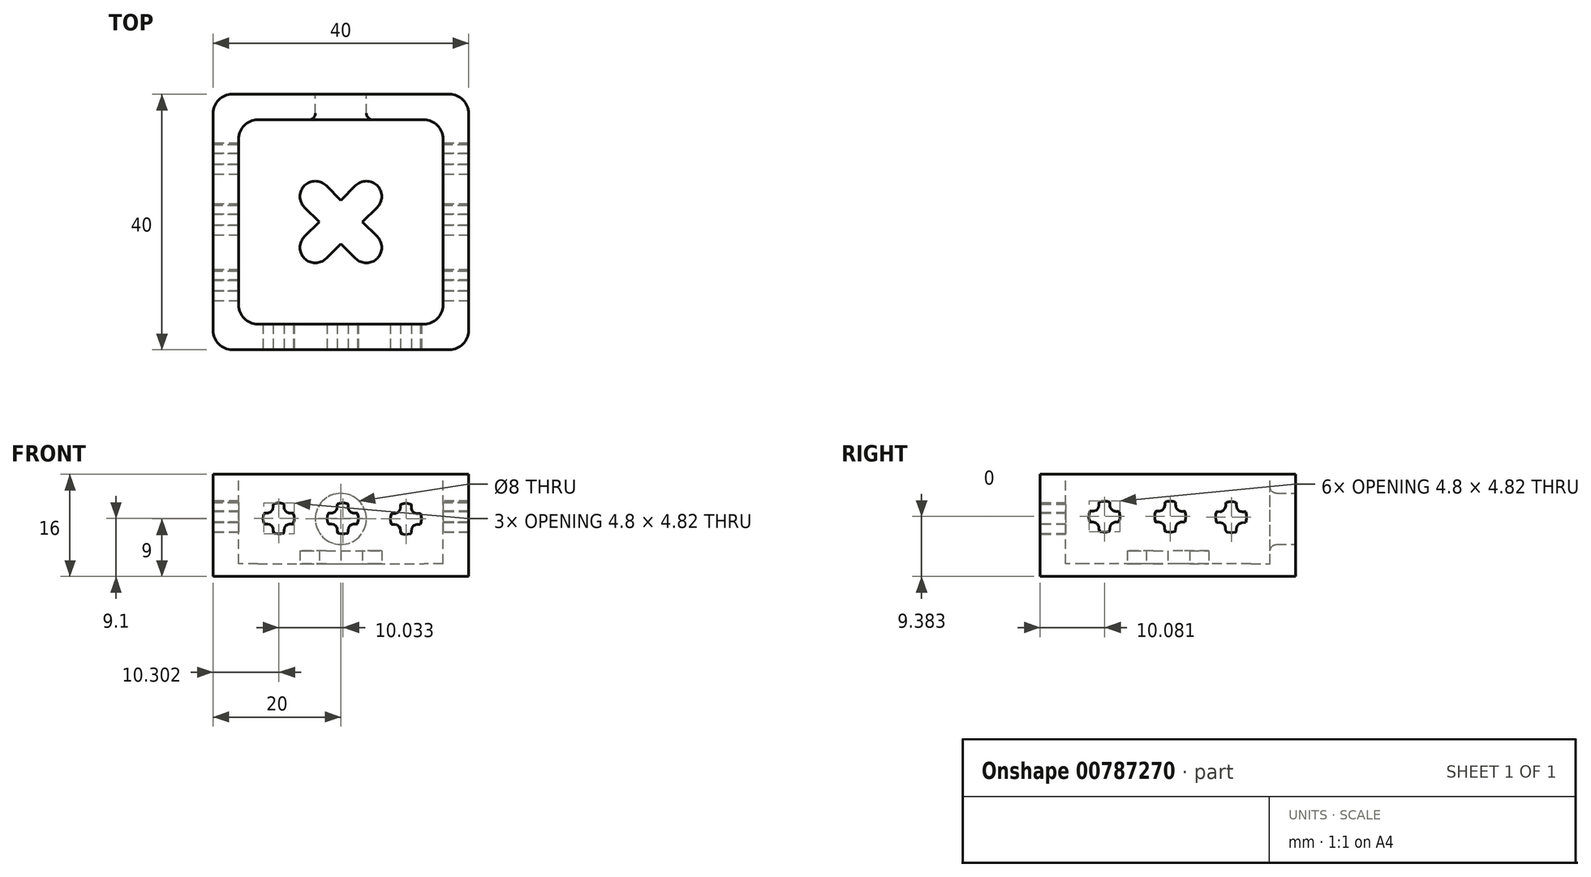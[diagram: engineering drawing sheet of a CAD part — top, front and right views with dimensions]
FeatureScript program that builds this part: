
annotation { "Feature Type Name" : "Feature", "Feature Type Description" : "" }
export const myFeature = defineFeature(function(context is Context, id is Id, definition is map)
    precondition{}
    {
        {
            var Q0;
            Q0=qCreatedBy(makeId("Top.planeOp"),FACE);
            var sketch = newSketch(context, id + "F0", { "sketchPlane" : qUnion([Q0])});
            skArc(sketch, "E0", {"start": v(1.7, 1.7) * mm, "mid": v(-1.7, 1.7) * mm, "end": v(-1.7, -1.7) * mm});
            skArc(sketch, "E1", {"start": v(9.7, -1.7) * mm, "mid": v(9.7, 1.7) * mm, "end": v(6.3, 1.7) * mm});
            skArc(sketch, "E2", {"start": v(6.3, -9.7) * mm, "mid": v(9.7, -9.7) * mm, "end": v(9.7, -6.3) * mm});
            skArc(sketch, "E3", {"start": v(-1.7, -6.3) * mm, "mid": v(-1.7, -9.7) * mm, "end": v(1.7, -9.7) * mm});
            skLineSegment(sketch, "E4", {"start": v(-1.7, -6.3) * mm, "end": v(0.6, -4) * mm});
            skLineSegment(sketch, "E5", {"start": v(9.7, -6.3) * mm, "end": v(7.4, -4) * mm});
            skLineSegment(sketch, "E6", {"start": v(-1.7, -1.7) * mm, "end": v(0.6, -4) * mm});
            skLineSegment(sketch, "E7", {"start": v(1.7, -9.7) * mm, "end": v(4, -7.4) * mm});
            skLineSegment(sketch, "E8.trimOffspring", {"start": v(4, -7.4) * mm, "end": v(6.3, -9.7) * mm});
            skLineSegment(sketch, "E9.trimOffspring", {"start": v(4, -0.6) * mm, "end": v(6.3, 1.7) * mm});
            skLineSegment(sketch, "E10.trimOffspring", {"start": v(4, -0.6) * mm, "end": v(1.7, 1.7) * mm});
            skLineSegment(sketch, "E11.trimOffspring", {"start": v(7.4, -4) * mm, "end": v(9.7, -1.7) * mm});
            skSolve(sketch);
        }
        {
            var Q0;
            Q0=makeQuery(id+"F0.imprint","IMPRINT",FACE,{"disambiguationData":[TD([[makeQuery(id+"F0.imprint","IMPRINT",EDGE,{"derivedFrom":sQuery(id+"F0.wireOp",EDGE,"E0")}),1.0]])]});
            extrude(context, id + "F1", {"entities" : qUnion([Q0]), "depth" : 2 * mm, "offsetDistance" : 25 * mm});
        }
        {
            var Q0;
            Q0=qCreatedBy(makeId("Top.planeOp"),FACE);
            var sketch = newSketch(context, id + "F2", { "sketchPlane" : qUnion([Q0])});
            skLineSegment(sketch, "E12.bottom", {"start": v(-9, 12) * mm, "end": v(17, 12) * mm});
            skLineSegment(sketch, "E12.top", {"start": v(-9, -20) * mm, "end": v(17, -20) * mm});
            skLineSegment(sketch, "E12.left", {"start": v(-12, 9) * mm, "end": v(-12, -17) * mm});
            skLineSegment(sketch, "E12.right", {"start": v(20, 9) * mm, "end": v(20, -17) * mm});
            skLineSegment(sketch, "E13", {"start": v(0.6, -4) * mm, "end": v(7.4, -4) * mm});
            skLineSegment(sketch, "E14", {"start": v(4, -0.6) * mm, "end": v(4, -7.4) * mm});
            skPoint(sketch, "E15", {"position": v(4, -4) * mm});
            skPoint(sketch, "E16", {"position": v(-12, -4) * mm});
            skPoint(sketch, "E17", {"position": v(4, 12) * mm});
            skPoint(sketch, "E18.visualSharp", {"position": v(20, 12) * mm});
            skArc(sketch, "E18.filletArc", {"start": v(20, 9) * mm, "mid": v(19.12, 11.12) * mm, "end": v(17, 12) * mm});
            skPoint(sketch, "E19.visualSharp", {"position": v(20, -20) * mm});
            skArc(sketch, "E19.filletArc", {"start": v(17, -20) * mm, "mid": v(19.12, -19.12) * mm, "end": v(20, -17) * mm});
            skPoint(sketch, "E20.visualSharp", {"position": v(-12, 12) * mm});
            skArc(sketch, "E20.filletArc", {"start": v(-9, 12) * mm, "mid": v(-11.12, 11.12) * mm, "end": v(-12, 9) * mm});
            skPoint(sketch, "E21.visualSharp", {"position": v(-12, -20) * mm});
            skArc(sketch, "E21.filletArc", {"start": v(-12, -17) * mm, "mid": v(-11.12, -19.12) * mm, "end": v(-9, -20) * mm});
            skLineSegment(sketch, "E22.bottom", {"start": v(-16, 16) * mm, "end": v(24, 16) * mm});
            skLineSegment(sketch, "E22.top", {"start": v(-16, -24) * mm, "end": v(24, -24) * mm});
            skLineSegment(sketch, "E22.left", {"start": v(-16, 16) * mm, "end": v(-16, -24) * mm});
            skLineSegment(sketch, "E22.right", {"start": v(24, 16) * mm, "end": v(24, -24) * mm});
            skPoint(sketch, "E23", {"position": v(-16, -4) * mm});
            skPoint(sketch, "E24", {"position": v(24, -4) * mm});
            skPoint(sketch, "E25", {"position": v(4, 16) * mm});
            skSolve(sketch);
        }
        {
            var Q0;
            Q0=makeQuery(id+"F2.imprint","IMPRINT",FACE,{"disambiguationData":[TD([[makeQuery(id+"F2.imprint","IMPRINT",EDGE,{"derivedFrom":sQuery(id+"F2.wireOp",EDGE,"E12.bottom")}),1.0]])]});
            extrude(context, id + "F3", {"entities" : qUnion([Q0]), "oppositeDirection" : true, "depth" : 2 * mm, "offsetDistance" : 25 * mm, "hasSecondDirection" : true, "secondDirectionOppositeDirection" : false, "secondDirectionDepth" : 14 * mm});
        }
        {
            var Q0;
            Q0=makeQuery(id+"F2.imprint","IMPRINT",FACE,{"disambiguationData":[TD([[makeQuery(id+"F2.imprint","IMPRINT",EDGE,{"derivedFrom":sQuery(id+"F2.wireOp",EDGE,"E12.bottom")}),-1.0]])]});
            var Q1;
            Q1=sQuery(id+"F2.wireOp",EDGE,"E20.filletArc");
            var Q2;
            Q2=sQuery(id+"F2.wireOp",EDGE,"E12.bottom");
            var Q3;
            Q3=sQuery(id+"F2.wireOp",EDGE,"E18.filletArc");
            var Q4;
            Q4=sQuery(id+"F2.wireOp",EDGE,"E12.right");
            var Q5;
            Q5=sQuery(id+"F2.wireOp",EDGE,"E19.filletArc");
            var Q6;
            Q6=sQuery(id+"F2.wireOp",EDGE,"E12.top");
            var Q7;
            Q7=sQuery(id+"F2.wireOp",EDGE,"E21.filletArc");
            var Q8;
            Q8=sQuery(id+"F2.wireOp",EDGE,"E12.left");
            extrude(context, id + "F4", {"entities" : qUnion([Q0]), "operationType" : NewBodyOperationType.ADD, "surfaceEntities" : qUnion([Q1, Q2, Q3, Q4, Q5, Q6, Q7, Q8]), "oppositeDirection" : true, "depth" : 2 * mm, "offsetDistance" : 25 * mm});
        }
        {
            var Q0;
            Q0=makeQuery(id+"F3.opExtrude","SWEPT_EDGE",EDGE,{"disambiguationData":[OSD([sQuery(id+"F2.wireOp",EDGE,"E22.top"),sQuery(id+"F2.wireOp",EDGE,"E22.left")])]});
            var Q1;
            Q1=makeQuery(id+"F3.opExtrude","SWEPT_EDGE",EDGE,{"disambiguationData":[OSD([sQuery(id+"F2.wireOp",EDGE,"E22.bottom"),sQuery(id+"F2.wireOp",EDGE,"E22.left")])]});
            var Q2;
            Q2=makeQuery(id+"F3.opExtrude","SWEPT_EDGE",EDGE,{"disambiguationData":[OSD([sQuery(id+"F2.wireOp",EDGE,"E22.bottom"),sQuery(id+"F2.wireOp",EDGE,"E22.right")])]});
            var Q3;
            Q3=makeQuery(id+"F3.opExtrude","SWEPT_EDGE",EDGE,{"disambiguationData":[OSD([sQuery(id+"F2.wireOp",EDGE,"E22.top"),sQuery(id+"F2.wireOp",EDGE,"E22.right")])]});
            fillet(context, id + "F5", {"entities" : qUnion([Q0, Q1, Q2, Q3]), "radius" : 3 * mm, "tangentPropagation" : true, "allowEdgeOverflow" : false});
        }
        {
            var Q0;
            Q0=makeQuery(id+"F3.opExtrude","SWEPT_FACE",FACE,{"disambiguationData":[OSD([sQuery(id+"F2.wireOp",EDGE,"E22.bottom")])]});
            var sketch = newSketch(context, id + "F6", { "sketchPlane" : qUnion([Q0])});
            skCircle(sketch, "E26", {"center": v(-4, 7) * mm, "radius": 4 * mm});
            skLineSegment(sketch, "E27", {"start": v(-20, 0) * mm, "end": v(-20, 14) * mm});
            skPoint(sketch, "E28", {"position": v(-20, 7) * mm});
            skLineSegment(sketch, "E29", {"start": v(-24, 14) * mm, "end": v(16, 14) * mm});
            skPoint(sketch, "E30", {"position": v(-4, 14) * mm});
            skSolve(sketch);
        }
        {
            var Q0;
            Q0=makeQuery(id+"F6.imprint","IMPRINT",FACE,{"disambiguationData":[TD([[makeQuery(id+"F6.imprint","IMPRINT",EDGE,{"derivedFrom":sQuery(id+"F6.wireOp",EDGE,"E26")}),1.0]])]});
            extrude(context, id + "F7", {"entities" : qUnion([Q0]), "operationType" : NewBodyOperationType.REMOVE, "oppositeDirection" : true, "depth" : 25 * mm, "offsetDistance" : 25 * mm});
        }
        {
            var Q0;
            Q0=makeQuery(id+"F7.boolean.opBoolean","COPY",EDGE,{"derivedFrom":makeQuery(id+"F7.opExtrude","CAP_EDGE",EDGE,{"disambiguationData":[OSD([sQuery(id+"F6.wireOp",EDGE,"E26")])],"isStart":true})});
            var Q1;
            Q1=makeQuery(id+"F7.boolean.opBoolean","INTERSECT",EDGE,{"derivedFrom":[makeQuery(id+"F3.opExtrude","SWEPT_FACE",FACE,{"disambiguationData":[OSD([sQuery(id+"F2.wireOp",EDGE,"E12.bottom")])]}),makeQuery(id+"F7.opExtrude","SWEPT_FACE",FACE,{"disambiguationData":[OSD([sQuery(id+"F6.wireOp",EDGE,"E26")])]})]});
            fillet(context, id + "F8", {"entities" : qUnion([Q0, Q1]), "radius" : 1 * mm, "tangentPropagation" : true, "allowEdgeOverflow" : false});
        }
        {
            var Q0;
            Q0=makeQuery(id+"F3.opExtrude","SWEPT_FACE",FACE,{"disambiguationData":[OSD([sQuery(id+"F2.wireOp",EDGE,"E22.top")])]});
            var sketch = newSketch(context, id + "F9", { "sketchPlane" : qUnion([Q0])});
            skFitSpline(sketch, "E31", {"points": [v(-6.58, 9.34) * mm, v(-5.7, 9.51) * mm, v(-4.88, 9.34) * mm], "startDerivative": vector(1.75, 0.5) * mm, "endDerivative": vector(1.65, -0.5) * mm});
            skFitSpline(sketch, "E32", {"points": [v(-4.88, 9.34) * mm, v(-4.88, 8.78) * mm, v(-4.74, 8.34) * mm, v(-4.42, 8.05) * mm, v(-4.08, 7.93) * mm, v(-3.66, 7.92) * mm, v(-3.46, 7.92) * mm, v(-3.38, 7.68) * mm, v(-3.3, 7.3) * mm, v(-3.3, 6.95) * mm, v(-3.34, 6.64) * mm, v(-3.46, 6.22) * mm], "startDerivative": vector(-0.26, -5.18) * mm, "endDerivative": vector(-1.41, -4.37) * mm});
            skFitSpline(sketch, "E33", {"points": [v(-6.58, 9.34) * mm, v(-6.58, 9.05) * mm, v(-6.59, 8.8) * mm, v(-6.61, 8.61) * mm, v(-6.79, 8.27) * mm, v(-6.98, 8.09) * mm, v(-7.24, 7.96) * mm, v(-7.56, 7.92) * mm, v(-8, 7.92) * mm, v(-8.1, 7.64) * mm, v(-8.15, 7.36) * mm, v(-8.17, 7.03) * mm, v(-8.14, 6.74) * mm, v(-8.09, 6.47) * mm, v(-8, 6.22) * mm, v(-7.81, 6.22) * mm, v(-7.5, 6.22) * mm, v(-7.25, 6.19) * mm, v(-7.06, 6.1) * mm, v(-6.84, 5.93) * mm, v(-6.73, 5.8) * mm, v(-6.64, 5.61) * mm, v(-6.59, 5.37) * mm, v(-6.58, 5.12) * mm, v(-6.58, 4.8) * mm, v(-6.33, 4.72) * mm, v(-5.98, 4.66) * mm, v(-5.7, 4.65) * mm, v(-5.43, 4.67) * mm, v(-5.07, 4.74) * mm, v(-4.88, 4.8) * mm, v(-4.88, 5.12) * mm, v(-4.88, 5.4) * mm, v(-4.78, 5.73) * mm, v(-4.64, 5.92) * mm, v(-4.37, 6.12) * mm, v(-3.96, 6.22) * mm, v(-3.46, 6.22) * mm], "startDerivative": vector(-0.02, -10.87) * mm, "endDerivative": vector(14.17, -0.52) * mm});
            skFitSpline(sketch, "E34", {"points": [v(3.45, 9.34) * mm, v(4.33, 9.51) * mm, v(5.15, 9.34) * mm], "startDerivative": vector(1.75, 0.5) * mm, "endDerivative": vector(1.65, -0.5) * mm});
            skFitSpline(sketch, "E35", {"points": [v(5.15, 9.34) * mm, v(5.15, 8.78) * mm, v(5.3, 8.34) * mm, v(5.61, 8.05) * mm, v(5.95, 7.93) * mm, v(6.37, 7.92) * mm, v(6.57, 7.92) * mm, v(6.65, 7.68) * mm, v(6.73, 7.3) * mm, v(6.73, 6.95) * mm, v(6.7, 6.64) * mm, v(6.57, 6.22) * mm], "startDerivative": vector(-0.26, -5.18) * mm, "endDerivative": vector(-1.41, -4.37) * mm});
            skFitSpline(sketch, "E36", {"points": [v(3.45, 9.34) * mm, v(3.45, 9.05) * mm, v(3.45, 8.8) * mm, v(3.42, 8.61) * mm, v(3.25, 8.27) * mm, v(3.05, 8.09) * mm, v(2.79, 7.96) * mm, v(2.47, 7.92) * mm, v(2.03, 7.92) * mm, v(1.94, 7.64) * mm, v(1.88, 7.36) * mm, v(1.86, 7.03) * mm, v(1.89, 6.74) * mm, v(1.95, 6.47) * mm, v(2.03, 6.22) * mm, v(2.22, 6.22) * mm, v(2.54, 6.22) * mm, v(2.79, 6.19) * mm, v(2.97, 6.1) * mm, v(3.2, 5.93) * mm, v(3.3, 5.8) * mm, v(3.4, 5.61) * mm, v(3.45, 5.37) * mm, v(3.45, 5.12) * mm, v(3.45, 4.8) * mm, v(3.7, 4.72) * mm, v(4.05, 4.66) * mm, v(4.33, 4.65) * mm, v(4.6, 4.67) * mm, v(4.96, 4.74) * mm, v(5.15, 4.8) * mm, v(5.15, 5.12) * mm, v(5.15, 5.4) * mm, v(5.25, 5.73) * mm, v(5.4, 5.92) * mm, v(5.66, 6.12) * mm, v(6.07, 6.22) * mm, v(6.57, 6.22) * mm], "startDerivative": vector(-0.02, -10.87) * mm, "endDerivative": vector(14.17, -0.52) * mm});
            skFitSpline(sketch, "E37", {"points": [v(13.33, 9.26) * mm, v(14.21, 9.43) * mm, v(15.03, 9.26) * mm], "startDerivative": vector(1.75, 0.5) * mm, "endDerivative": vector(1.65, -0.5) * mm});
            skFitSpline(sketch, "E38", {"points": [v(15.03, 9.26) * mm, v(15.03, 8.7) * mm, v(15.18, 8.27) * mm, v(15.5, 7.97) * mm, v(15.83, 7.85) * mm, v(16.25, 7.84) * mm, v(16.45, 7.84) * mm, v(16.53, 7.6) * mm, v(16.6, 7.22) * mm, v(16.61, 6.88) * mm, v(16.57, 6.56) * mm, v(16.45, 6.14) * mm], "startDerivative": vector(-0.26, -5.18) * mm, "endDerivative": vector(-1.41, -4.37) * mm});
            skFitSpline(sketch, "E39", {"points": [v(13.33, 9.26) * mm, v(13.33, 8.97) * mm, v(13.33, 8.72) * mm, v(13.3, 8.53) * mm, v(13.13, 8.2) * mm, v(12.93, 8) * mm, v(12.67, 7.88) * mm, v(12.35, 7.84) * mm, v(11.9, 7.84) * mm, v(11.82, 7.56) * mm, v(11.76, 7.28) * mm, v(11.74, 6.95) * mm, v(11.77, 6.66) * mm, v(11.83, 6.4) * mm, v(11.9, 6.14) * mm, v(12.1, 6.14) * mm, v(12.42, 6.14) * mm, v(12.66, 6.1) * mm, v(12.85, 6.03) * mm, v(13.08, 5.85) * mm, v(13.18, 5.71) * mm, v(13.27, 5.54) * mm, v(13.33, 5.29) * mm, v(13.33, 5.04) * mm, v(13.33, 4.72) * mm, v(13.58, 4.64) * mm, v(13.93, 4.58) * mm, v(14.21, 4.57) * mm, v(14.48, 4.59) * mm, v(14.84, 4.66) * mm, v(15.03, 4.72) * mm, v(15.03, 5.04) * mm, v(15.03, 5.32) * mm, v(15.13, 5.65) * mm, v(15.27, 5.84) * mm, v(15.54, 6.04) * mm, v(15.95, 6.14) * mm, v(16.45, 6.14) * mm], "startDerivative": vector(-0.02, -10.87) * mm, "endDerivative": vector(14.17, -0.52) * mm});
            skSolve(sketch);
        }
        {
            var Q0;
            Q0=makeQuery(id+"F9.imprint","IMPRINT",FACE,{"disambiguationData":[TD([[makeQuery(id+"F9.imprint","IMPRINT",EDGE,{"derivedFrom":sQuery(id+"F9.wireOp",EDGE,"E31")}),-1.0]])]});
            var Q1;
            Q1=makeQuery(id+"F9.imprint","IMPRINT",FACE,{"disambiguationData":[TD([[makeQuery(id+"F9.imprint","IMPRINT",EDGE,{"derivedFrom":sQuery(id+"F9.wireOp",EDGE,"E34")}),-1.0]])]});
            var Q2;
            Q2=makeQuery(id+"F9.imprint","IMPRINT",FACE,{"disambiguationData":[TD([[makeQuery(id+"F9.imprint","IMPRINT",EDGE,{"derivedFrom":sQuery(id+"F9.wireOp",EDGE,"E37")}),-1.0]])]});
            var Q3;
            Q3=sQuery(id+"F9.wireOp",EDGE,"E39");
            var Q4;
            Q4=sQuery(id+"F9.wireOp",EDGE,"E36");
            var Q5;
            Q5=sQuery(id+"F9.wireOp",EDGE,"E35");
            var Q6;
            Q6=sQuery(id+"F9.wireOp",EDGE,"E33");
            var Q7;
            Q7=sQuery(id+"F9.wireOp",EDGE,"E38");
            var Q8;
            Q8=sQuery(id+"F9.wireOp",EDGE,"E34");
            var Q9;
            Q9=sQuery(id+"F9.wireOp",EDGE,"E32");
            var Q10;
            Q10=sQuery(id+"F9.wireOp",EDGE,"E31");
            var Q11;
            Q11=sQuery(id+"F9.wireOp",EDGE,"E37");
            extrude(context, id + "F10", {"entities" : qUnion([Q0, Q1, Q2]), "operationType" : NewBodyOperationType.REMOVE, "surfaceEntities" : qUnion([Q3, Q4, Q5, Q6, Q7, Q8, Q9, Q10, Q11]), "oppositeDirection" : true, "depth" : 25 * mm, "offsetDistance" : 25 * mm});
        }
        {
            var Q0;
            Q0=makeQuery(id+"F3.opExtrude","SWEPT_FACE",FACE,{"disambiguationData":[OSD([sQuery(id+"F2.wireOp",EDGE,"E22.right")])]});
            var sketch = newSketch(context, id + "F11", { "sketchPlane" : qUnion([Q0])});
            skFitSpline(sketch, "E40", {"points": [v(-14.8, 9.63) * mm, v(-13.92, 9.8) * mm, v(-13.1, 9.63) * mm], "startDerivative": vector(1.75, 0.5) * mm, "endDerivative": vector(1.65, -0.5) * mm});
            skFitSpline(sketch, "E41", {"points": [v(-13.1, 9.63) * mm, v(-13.1, 9.06) * mm, v(-12.96, 8.63) * mm, v(-12.64, 8.33) * mm, v(-12.3, 8.21) * mm, v(-11.88, 8.2) * mm, v(-11.68, 8.2) * mm, v(-11.6, 7.96) * mm, v(-11.53, 7.58) * mm, v(-11.52, 7.24) * mm, v(-11.56, 6.92) * mm, v(-11.68, 6.5) * mm], "startDerivative": vector(-0.26, -5.18) * mm, "endDerivative": vector(-1.41, -4.37) * mm});
            skFitSpline(sketch, "E42", {"points": [v(-14.8, 9.63) * mm, v(-14.8, 9.33) * mm, v(-14.8, 9.09) * mm, v(-14.84, 8.9) * mm, v(-15, 8.55) * mm, v(-15.2, 8.37) * mm, v(-15.47, 8.24) * mm, v(-15.78, 8.2) * mm, v(-16.23, 8.2) * mm, v(-16.31, 7.93) * mm, v(-16.37, 7.64) * mm, v(-16.4, 7.31) * mm, v(-16.37, 7.02) * mm, v(-16.3, 6.76) * mm, v(-16.23, 6.5) * mm, v(-16.03, 6.5) * mm, v(-15.72, 6.5) * mm, v(-15.47, 6.47) * mm, v(-15.28, 6.39) * mm, v(-15.06, 6.22) * mm, v(-14.95, 6.08) * mm, v(-14.86, 5.9) * mm, v(-14.8, 5.65) * mm, v(-14.8, 5.4) * mm, v(-14.8, 5.09) * mm, v(-14.55, 5) * mm, v(-14.2, 4.94) * mm, v(-13.92, 4.93) * mm, v(-13.66, 4.95) * mm, v(-13.29, 5.02) * mm, v(-13.1, 5.09) * mm, v(-13.1, 5.4) * mm, v(-13.1, 5.68) * mm, v(-13, 6) * mm, v(-12.86, 6.2) * mm, v(-12.6, 6.4) * mm, v(-12.18, 6.5) * mm, v(-11.68, 6.5) * mm], "startDerivative": vector(-0.02, -10.87) * mm, "endDerivative": vector(14.17, -0.52) * mm});
            skFitSpline(sketch, "E43", {"points": [v(-4.5, 9.63) * mm, v(-3.62, 9.8) * mm, v(-2.8, 9.63) * mm], "startDerivative": vector(1.75, 0.5) * mm, "endDerivative": vector(1.65, -0.5) * mm});
            skFitSpline(sketch, "E44", {"points": [v(-2.8, 9.63) * mm, v(-2.8, 9.06) * mm, v(-2.65, 8.63) * mm, v(-2.34, 8.33) * mm, v(-2, 8.21) * mm, v(-1.58, 8.2) * mm, v(-1.38, 8.2) * mm, v(-1.3, 7.96) * mm, v(-1.23, 7.58) * mm, v(-1.22, 7.24) * mm, v(-1.26, 6.92) * mm, v(-1.38, 6.5) * mm], "startDerivative": vector(-0.26, -5.18) * mm, "endDerivative": vector(-1.41, -4.37) * mm});
            skFitSpline(sketch, "E45", {"points": [v(-4.5, 9.63) * mm, v(-4.5, 9.33) * mm, v(-4.5, 9.09) * mm, v(-4.53, 8.9) * mm, v(-4.7, 8.55) * mm, v(-4.9, 8.37) * mm, v(-5.16, 8.24) * mm, v(-5.48, 8.2) * mm, v(-5.92, 8.2) * mm, v(-6.01, 7.93) * mm, v(-6.07, 7.64) * mm, v(-6.09, 7.31) * mm, v(-6.06, 7.02) * mm, v(-6, 6.76) * mm, v(-5.92, 6.5) * mm, v(-5.73, 6.5) * mm, v(-5.41, 6.5) * mm, v(-5.17, 6.47) * mm, v(-4.98, 6.39) * mm, v(-4.75, 6.22) * mm, v(-4.65, 6.08) * mm, v(-4.56, 5.9) * mm, v(-4.5, 5.65) * mm, v(-4.5, 5.4) * mm, v(-4.5, 5.09) * mm, v(-4.25, 5) * mm, v(-3.9, 4.94) * mm, v(-3.62, 4.93) * mm, v(-3.35, 4.95) * mm, v(-2.99, 5.02) * mm, v(-2.8, 5.09) * mm, v(-2.8, 5.4) * mm, v(-2.8, 5.68) * mm, v(-2.7, 6) * mm, v(-2.56, 6.2) * mm, v(-2.3, 6.4) * mm, v(-1.88, 6.5) * mm, v(-1.38, 6.5) * mm], "startDerivative": vector(-0.02, -10.87) * mm, "endDerivative": vector(14.17, -0.52) * mm});
            skFitSpline(sketch, "E46", {"points": [v(5.03, 9.55) * mm, v(5.91, 9.72) * mm, v(6.73, 9.55) * mm], "startDerivative": vector(1.75, 0.5) * mm, "endDerivative": vector(1.65, -0.5) * mm});
            skFitSpline(sketch, "E47", {"points": [v(6.73, 9.55) * mm, v(6.73, 8.98) * mm, v(6.88, 8.55) * mm, v(7.2, 8.25) * mm, v(7.53, 8.14) * mm, v(7.95, 8.13) * mm, v(8.15, 8.13) * mm, v(8.23, 7.88) * mm, v(8.3, 7.5) * mm, v(8.31, 7.16) * mm, v(8.27, 6.84) * mm, v(8.15, 6.43) * mm], "startDerivative": vector(-0.26, -5.18) * mm, "endDerivative": vector(-1.41, -4.37) * mm});
            skFitSpline(sketch, "E48", {"points": [v(5.03, 9.55) * mm, v(5.03, 9.25) * mm, v(5.03, 9) * mm, v(5, 8.82) * mm, v(4.83, 8.48) * mm, v(4.63, 8.3) * mm, v(4.37, 8.17) * mm, v(4.05, 8.13) * mm, v(3.6, 8.13) * mm, v(3.52, 7.85) * mm, v(3.46, 7.56) * mm, v(3.44, 7.23) * mm, v(3.47, 6.95) * mm, v(3.53, 6.68) * mm, v(3.6, 6.43) * mm, v(3.8, 6.43) * mm, v(4.12, 6.43) * mm, v(4.36, 6.4) * mm, v(4.55, 6.31) * mm, v(4.78, 6.14) * mm, v(4.89, 6) * mm, v(4.97, 5.82) * mm, v(5.03, 5.57) * mm, v(5.03, 5.32) * mm, v(5.03, 5) * mm, v(5.29, 4.93) * mm, v(5.63, 4.87) * mm, v(5.91, 4.85) * mm, v(6.18, 4.87) * mm, v(6.54, 4.95) * mm, v(6.73, 5) * mm, v(6.73, 5.32) * mm, v(6.73, 5.6) * mm, v(6.83, 5.93) * mm, v(6.97, 6.13) * mm, v(7.24, 6.33) * mm, v(7.65, 6.43) * mm, v(8.15, 6.43) * mm], "startDerivative": vector(-0.02, -10.87) * mm, "endDerivative": vector(14.17, -0.52) * mm});
            skSolve(sketch);
        }
        {
            var Q0;
            Q0=makeQuery(id+"F11.imprint","IMPRINT",FACE,{"disambiguationData":[TD([[makeQuery(id+"F11.imprint","IMPRINT",EDGE,{"derivedFrom":sQuery(id+"F11.wireOp",EDGE,"E40")}),-1.0]])]});
            var Q1;
            Q1=makeQuery(id+"F11.imprint","IMPRINT",FACE,{"disambiguationData":[TD([[makeQuery(id+"F11.imprint","IMPRINT",EDGE,{"derivedFrom":sQuery(id+"F11.wireOp",EDGE,"E43")}),-1.0]])]});
            var Q2;
            Q2=makeQuery(id+"F11.imprint","IMPRINT",FACE,{"disambiguationData":[TD([[makeQuery(id+"F11.imprint","IMPRINT",EDGE,{"derivedFrom":sQuery(id+"F11.wireOp",EDGE,"E46")}),-1.0]])]});
            extrude(context, id + "F12", {"entities" : qUnion([Q0, Q1, Q2]), "operationType" : NewBodyOperationType.REMOVE, "oppositeDirection" : true, "depth" : 45.8 * mm, "offsetDistance" : 25 * mm});
        }
    });
